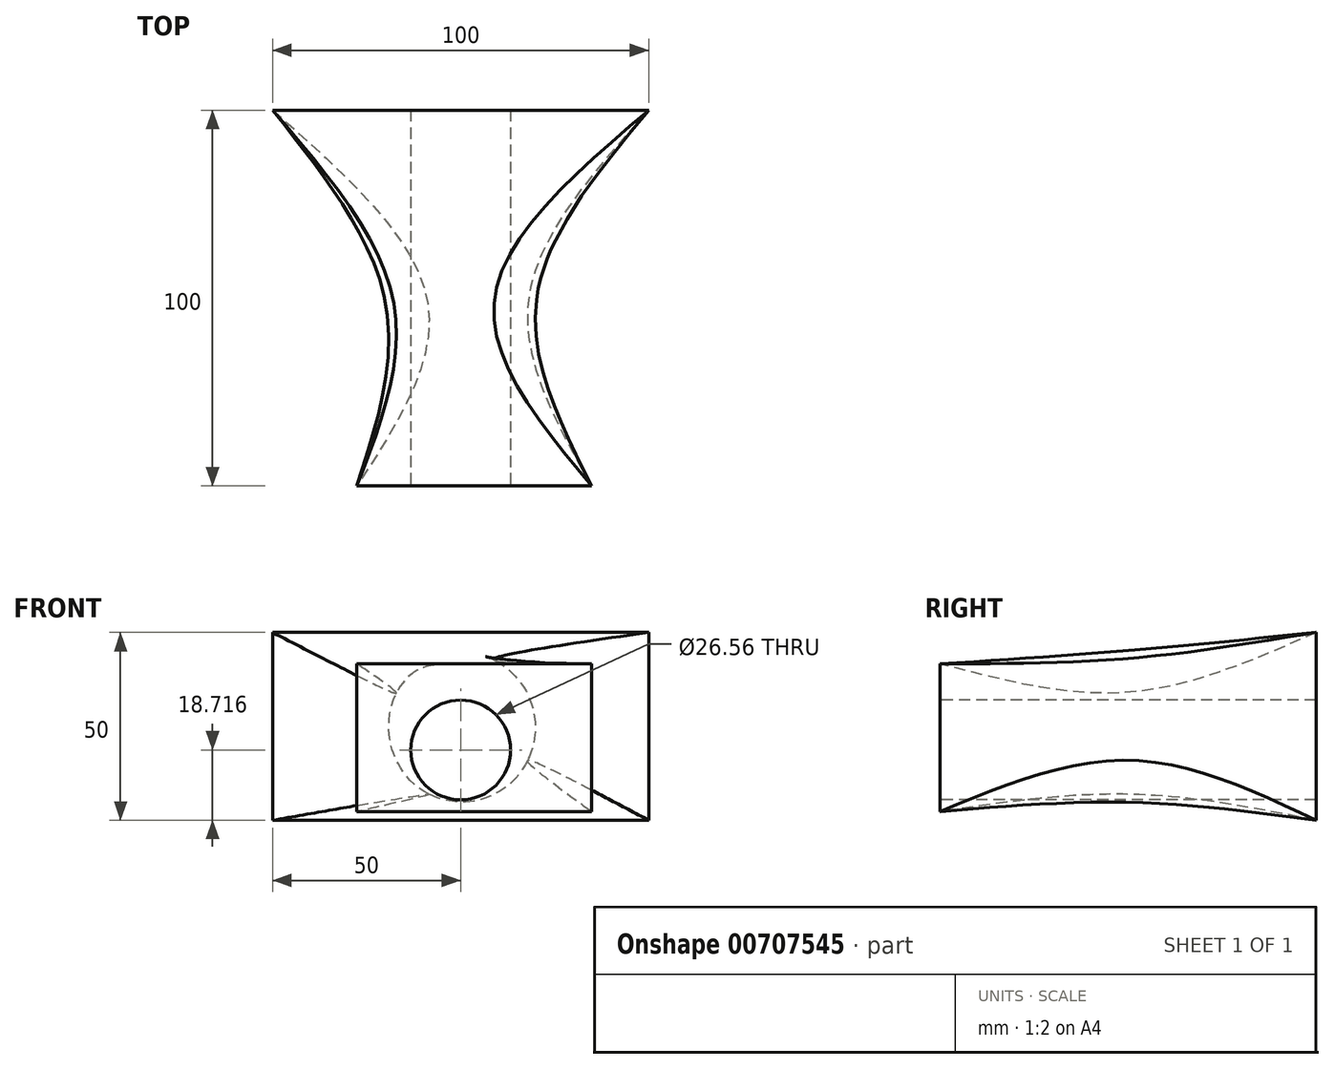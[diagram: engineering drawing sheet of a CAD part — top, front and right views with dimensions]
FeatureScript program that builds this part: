
annotation { "Feature Type Name" : "Feature", "Feature Type Description" : "" }
export const myFeature = defineFeature(function(context is Context, id is Id, definition is map)
    precondition{}
    {
        {
            var Q0;
            Q0=qCreatedBy(makeId("Front.planeOp"),FACE);
            var sketch = newSketch(context, id + "F0", { "sketchPlane" : qUnion([Q0])});
            skLineSegment(sketch, "E0.bottom", {"start": v(-50, 25) * mm, "end": v(50, 25) * mm});
            skLineSegment(sketch, "E0.top", {"start": v(-50, -25) * mm, "end": v(50, -25) * mm});
            skLineSegment(sketch, "E0.left", {"start": v(-50, 25) * mm, "end": v(-50, -25) * mm});
            skLineSegment(sketch, "E0.right", {"start": v(50, 25) * mm, "end": v(50, -25) * mm});
            skSolve(sketch);
        }
        {
            var Q0;
            Q0=qCreatedBy(makeId("Front.planeOp"),FACE);
            cPlane(context, id + "F1", {"entities" : qUnion([Q0]), "cplaneType" : CPlaneType.OFFSET, "offset" : 50 * mm, "width" : 150 * mm, "height" : 150 * mm});
        }
        {
            var Q0;
            Q0=qCreatedBy(id+"F1.planeOp",FACE);
            var sketch = newSketch(context, id + "F2", { "sketchPlane" : qUnion([Q0])});
            skCircle(sketch, "E1", {"center": v(0, 0) * mm, "radius": 20.22 * mm});
            skSolve(sketch);
        }
        {
            var Q0;
            Q0=qCreatedBy(makeId("Front.planeOp"),FACE);
            cPlane(context, id + "F3", {"entities" : qUnion([Q0]), "cplaneType" : CPlaneType.OFFSET, "offset" : 100 * mm, "width" : 150 * mm, "height" : 150 * mm});
        }
        {
            var Q0;
            Q0=qCreatedBy(id+"F3.planeOp",FACE);
            var sketch = newSketch(context, id + "F4", { "sketchPlane" : qUnion([Q0])});
            skLineSegment(sketch, "E2.bottom", {"start": v(-27.6, 16.62) * mm, "end": v(34.83, 16.62) * mm});
            skLineSegment(sketch, "E2.top", {"start": v(-27.6, -22.7) * mm, "end": v(34.83, -22.7) * mm});
            skLineSegment(sketch, "E2.left", {"start": v(-27.6, 16.62) * mm, "end": v(-27.6, -22.7) * mm});
            skLineSegment(sketch, "E2.right", {"start": v(34.83, 16.62) * mm, "end": v(34.83, -22.7) * mm});
            skSolve(sketch);
        }
        {
            var Q0;
            Q0=makeQuery(id+"F0.imprint","IMPRINT",FACE,{"disambiguationData":[TD([[makeQuery(id+"F0.imprint","IMPRINT",EDGE,{"derivedFrom":sQuery(id+"F0.wireOp",EDGE,"E0.bottom")}),-1.0]])]});
            var Q1;
            Q1=makeQuery(id+"F2.imprint","IMPRINT",FACE,{"disambiguationData":[TD([[makeQuery(id+"F2.imprint","IMPRINT",EDGE,{"derivedFrom":sQuery(id+"F2.wireOp",EDGE,"E1")}),1.0]])]});
            var Q2;
            Q2=makeQuery(id+"F4.imprint","IMPRINT",FACE,{"disambiguationData":[TD([[makeQuery(id+"F4.imprint","IMPRINT",EDGE,{"derivedFrom":sQuery(id+"F4.wireOp",EDGE,"E2.bottom")}),-1.0]])]});
            loft(context, id + "F5", {"sheetProfilesArray" : [{ "sheetProfileEntities" : qUnion([Q0]) }, { "sheetProfileEntities" : qUnion([Q1]) }, { "sheetProfileEntities" : qUnion([Q2]) }]});
        }
        {
            var Q0;
            Q0=makeQuery(id+"F5.opLoft","CAP_FACE",FACE,{"disambiguationData":[OSD([makeQuery(id+"F4.imprint","IMPRINT",FACE,{"disambiguationData":[TD([[makeQuery(id+"F4.imprint","IMPRINT",EDGE,{"derivedFrom":sQuery(id+"F4.wireOp",EDGE,"E2.bottom")}),-1.0]])]})])],"isStart":true});
            var sketch = newSketch(context, id + "F6", { "sketchPlane" : qUnion([Q0])});
            skCircle(sketch, "E3", {"center": v(0, -6.28) * mm, "radius": 13.28 * mm});
            skSolve(sketch);
        }
        {
            var Q0;
            Q0=makeQuery(id+"F6.imprint","IMPRINT",FACE,{"disambiguationData":[TD([[makeQuery(id+"F6.imprint","IMPRINT",EDGE,{"derivedFrom":sQuery(id+"F6.wireOp",EDGE,"E3")}),1.0]])]});
            extrude(context, id + "F7", {"entities" : qUnion([Q0]), "operationType" : NewBodyOperationType.REMOVE, "endBound" : BoundingType.UP_TO_NEXT, "oppositeDirection" : true, "depth" : 25 * mm, "offsetDistance" : 25 * mm});
        }
    });
